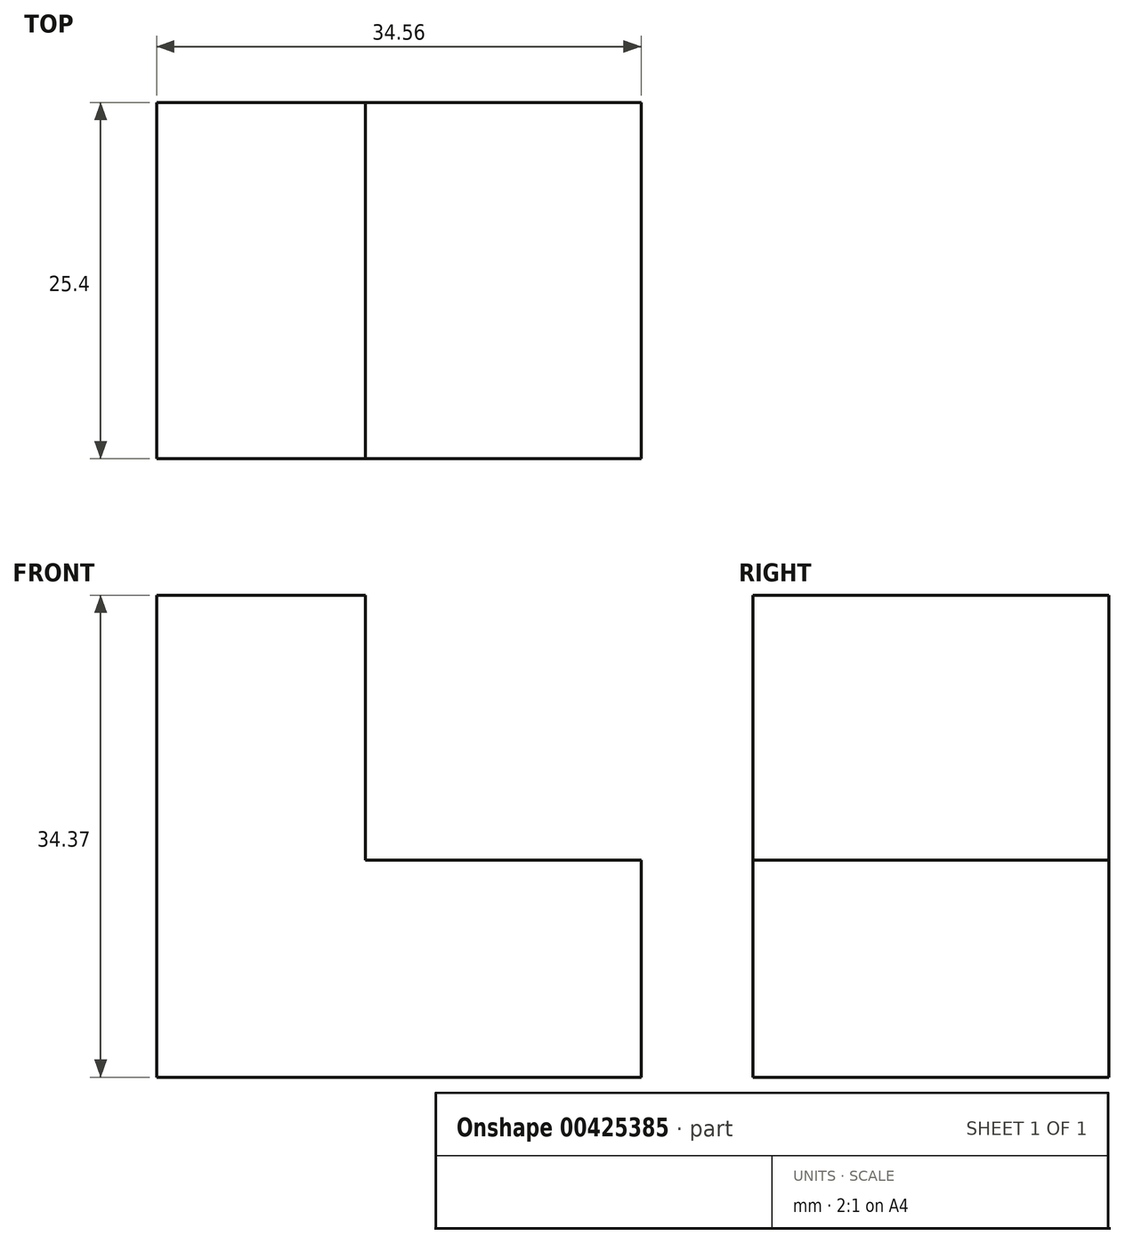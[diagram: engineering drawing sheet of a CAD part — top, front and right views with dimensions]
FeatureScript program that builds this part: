
annotation { "Feature Type Name" : "Feature", "Feature Type Description" : "" }
export const myFeature = defineFeature(function(context is Context, id is Id, definition is map)
    precondition{}
    {
        {
            var Q0;
            Q0=qCreatedBy(makeId("Front.planeOp"),FACE);
            var sketch = newSketch(context, id + "F0", { "sketchPlane" : qUnion([Q0])});
            skLineSegment(sketch, "E0", {"start": v(0, 0) * mm, "end": v(-34.56, 0) * mm});
            skLineSegment(sketch, "E1", {"start": v(-34.56, 0) * mm, "end": v(-34.56, 34.37) * mm});
            skLineSegment(sketch, "E2", {"start": v(-34.56, 34.37) * mm, "end": v(-19.67, 34.37) * mm});
            skLineSegment(sketch, "E3", {"start": v(-19.67, 34.37) * mm, "end": v(-19.67, 15.47) * mm});
            skLineSegment(sketch, "E4", {"start": v(-19.67, 15.47) * mm, "end": v(0, 15.47) * mm});
            skLineSegment(sketch, "E5", {"start": v(0, 15.47) * mm, "end": v(0, 0) * mm});
            skSolve(sketch);
        }
        {
            var Q0;
            Q0 = qSketchRegion(id + "F0", true);
            extrude(context, id + "F1", {"entities" : qUnion([Q0]), "depth" : 25.4 * mm});
        }
    });
